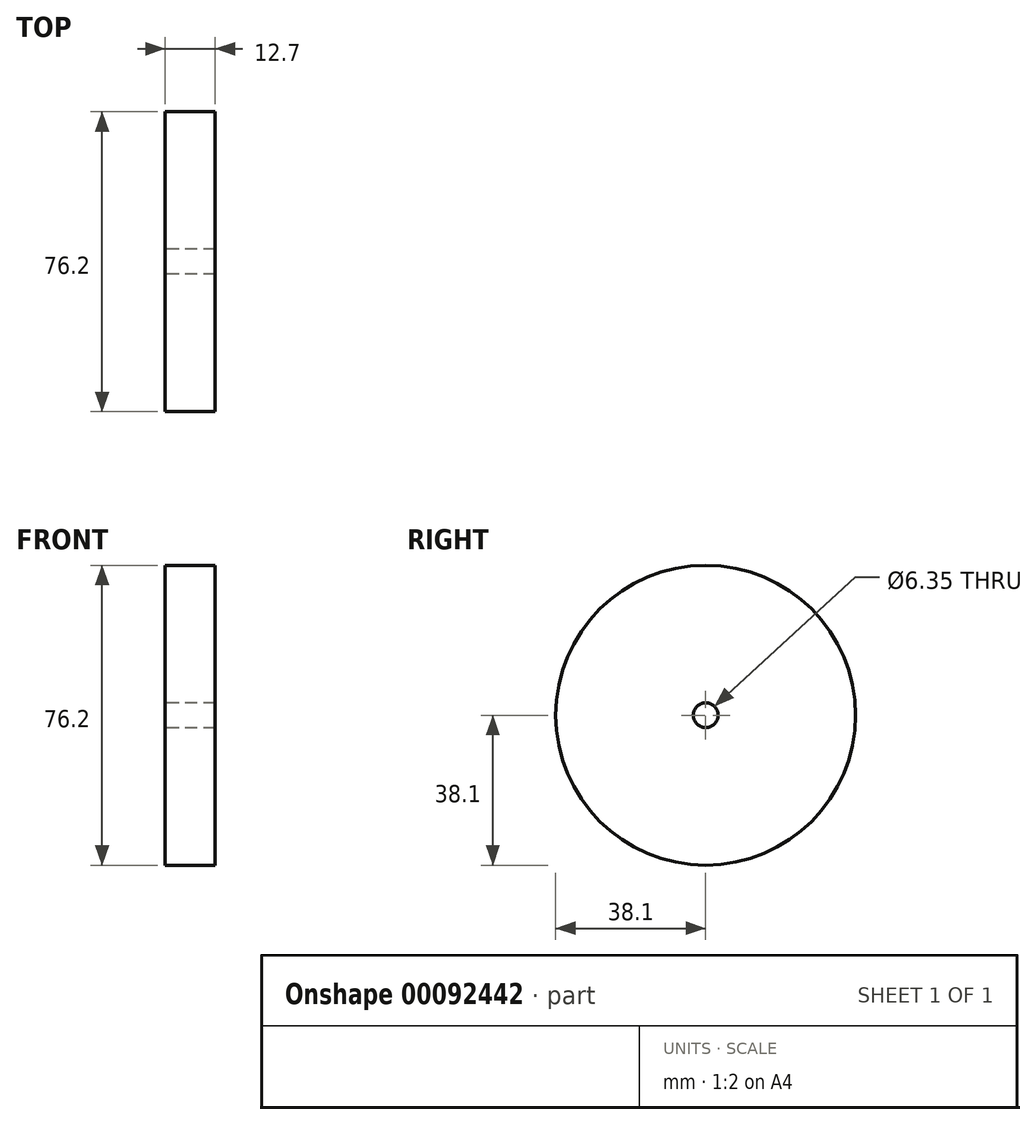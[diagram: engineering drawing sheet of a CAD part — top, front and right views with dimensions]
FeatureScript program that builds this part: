
annotation { "Feature Type Name" : "Feature", "Feature Type Description" : "" }
export const myFeature = defineFeature(function(context is Context, id is Id, definition is map)
    precondition{}
    {
        {
            var Q0;
            Q0=qCreatedBy(makeId("Right.planeOp"),FACE);
            var sketch = newSketch(context, id + "F0", { "sketchPlane" : qUnion([Q0])});
            skCircle(sketch, "E0", {"center": v(0, 0) * mm, "radius": 38.1 * mm});
            skCircle(sketch, "E1", {"center": v(0, 0) * mm, "radius": 3.18 * mm});
            skSolve(sketch);
        }
        {
            var Q0;
            Q0=makeQuery(id+"F0.imprint","IMPRINT",FACE,{"disambiguationData":[TD([[makeQuery(id+"F0.imprint","IMPRINT",EDGE,{"derivedFrom":sQuery(id+"F0.wireOp",EDGE,"E0")}),1.0]])]});
            extrude(context, id + "F1", {"entities" : qUnion([Q0]), "depth" : 12.7 * mm});
        }
    });
